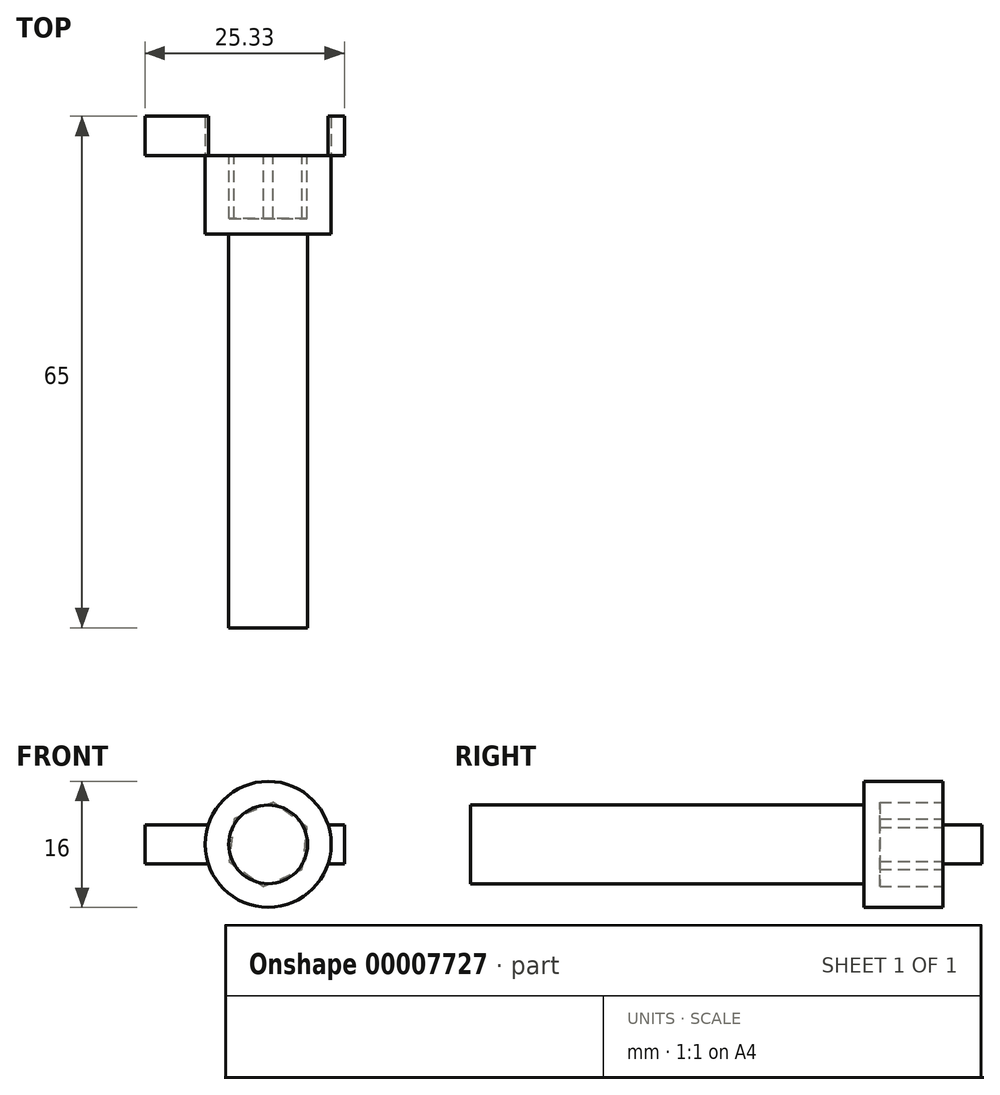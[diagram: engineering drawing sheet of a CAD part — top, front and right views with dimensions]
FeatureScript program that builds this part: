
annotation { "Feature Type Name" : "Feature", "Feature Type Description" : "" }
export const myFeature = defineFeature(function(context is Context, id is Id, definition is map)
    precondition{}
    {
        {
            var Q0;
            Q0=qCreatedBy(makeId("Right.planeOp"),FACE);
            var sketch = newSketch(context, id + "F0", { "sketchPlane" : qUnion([Q0])});
            skLineSegment(sketch, "E0", {"start": v(0, 0) * mm, "end": v(-60, 0) * mm});
            skLineSegment(sketch, "E1", {"start": v(-60, 0) * mm, "end": v(-60, 5) * mm});
            skLineSegment(sketch, "E2", {"start": v(-60, 5) * mm, "end": v(-10, 5) * mm});
            skLineSegment(sketch, "E3", {"start": v(-10, 5) * mm, "end": v(-10, 8) * mm});
            skLineSegment(sketch, "E4", {"start": v(-10, 8) * mm, "end": v(0, 8) * mm});
            skLineSegment(sketch, "E5", {"start": v(0, 8) * mm, "end": v(0, 0) * mm});
            skSolve(sketch);
        }
        {
            var Q0;
            Q0=makeQuery(id+"F0.imprint","IMPRINT",FACE,{"disambiguationData":[TD([[makeQuery(id+"F0.imprint","IMPRINT",EDGE,{"derivedFrom":sQuery(id+"F0.wireOp",EDGE,"E0")}),-1.0]])]});
            var Q1;
            Q1=sQuery(id+"F0.wireOp",EDGE,"E0");
            revolve(context, id + "F1", {"entities" : qUnion([Q0]), "axis" : qUnion([Q1]), "revolveType" : RevolveType.FULL});
        }
        {
            var Q0;
            Q0=makeQuery(id+"F1.opRevolve","SWEPT_FACE",FACE,{"disambiguationData":[OSD([sQuery(id+"F0.wireOp",EDGE,"E5")])]});
            var sketch = newSketch(context, id + "F2", { "sketchPlane" : qUnion([Q0])});
            skCircle(sketch, "E6.cCircle", {"center": v(0, 0) * mm, "radius": 4.67 * mm, "construction": true});
            skLineSegment(sketch, "E6.0", {"start": v(0.61, -5.35) * mm, "end": v(-4.33, -3.2) * mm});
            skLineSegment(sketch, "E6.1", {"start": v(-4.33, -3.2) * mm, "end": v(-4.94, 2.15) * mm});
            skLineSegment(sketch, "E6.2", {"start": v(-4.94, 2.15) * mm, "end": v(-0.61, 5.35) * mm});
            skLineSegment(sketch, "E6.3", {"start": v(-0.61, 5.35) * mm, "end": v(4.33, 3.2) * mm});
            skLineSegment(sketch, "E6.4", {"start": v(4.33, 3.2) * mm, "end": v(4.94, -2.15) * mm});
            skLineSegment(sketch, "E6.5", {"start": v(4.94, -2.15) * mm, "end": v(0.61, -5.35) * mm});
            skPoint(sketch, "E6.0.midPoint", {"position": v(-1.86, -4.28) * mm});
            skSolve(sketch);
        }
        {
            var Q0;
            Q0 = qSketchRegion(id + "F2", true);
            extrude(context, id + "F3", {"entities" : qUnion([Q0]), "operationType" : NewBodyOperationType.REMOVE, "oppositeDirection" : true, "depth" : 8 * mm});
        }
        {
            var Q0;
            Q0=makeQuery(id+"F1.opRevolve","SWEPT_FACE",FACE,{"disambiguationData":[OSD([sQuery(id+"F0.wireOp",EDGE,"E5")])]});
            var sketch = newSketch(context, id + "F4", { "sketchPlane" : qUnion([Q0])});
            skLineSegment(sketch, "E7.bottom", {"start": v(-9.69, 2.5) * mm, "end": v(15.64, 2.5) * mm});
            skLineSegment(sketch, "E7.top", {"start": v(-9.69, -2.5) * mm, "end": v(15.64, -2.5) * mm});
            skLineSegment(sketch, "E7.left", {"start": v(-9.69, 2.5) * mm, "end": v(-9.69, -2.5) * mm});
            skLineSegment(sketch, "E7.right", {"start": v(15.64, 2.5) * mm, "end": v(15.64, -2.5) * mm});
            skSolve(sketch);
        }
        {
            var Q0;
            {var subQ0=makeQuery(id+"F3.boolean.opBoolean","COPY",EDGE,{"derivedFrom":makeQuery(id+"F3.opExtrude","CAP_EDGE",EDGE,{"disambiguationData":[OSD([sQuery(id+"F2.wireOp",EDGE,"E6.2")])],"isStart":true})});var subQ3=makeQuery(id+"F3.boolean.opBoolean","COPY",EDGE,{"derivedFrom":makeQuery(id+"F3.opExtrude","CAP_EDGE",EDGE,{"disambiguationData":[OSD([sQuery(id+"F2.wireOp",EDGE,"E6.1")])],"isStart":true})});var subQ4=makeQuery(id+"F4.imprint","INTERSECT",VERTEX,{"derivedFrom":[subQ3,subQ0]});Q0=makeQuery(id+"F4.imprint","IMPRINT",FACE,{"disambiguationData":[TD([[makeQuery(id+"F4.imprint","IMPRINT",EDGE,{"disambiguationData":[TD([[subQ4,1.0]])],"derivedFrom":subQ3}),1.0]])]});}
            var Q1;
            {var subQ5=sQuery(id+"F4.wireOp",EDGE,"E7.left");Q1=makeQuery(id+"F4.imprint","IMPRINT",FACE,{"disambiguationData":[TD([[makeQuery(id+"F4.imprint","IMPRINT",EDGE,{"derivedFrom":subQ5}),1.0]])]});}
            var Q2;
            {var subQ5=makeQuery(id+"F3.boolean.opBoolean","COPY",EDGE,{"derivedFrom":makeQuery(id+"F3.opExtrude","CAP_EDGE",EDGE,{"disambiguationData":[OSD([sQuery(id+"F2.wireOp",EDGE,"E6.2")])],"isStart":true})});var subQ6=sQuery(id+"F4.wireOp",EDGE,"E7.bottom");var subQ7=makeQuery(id+"F4.imprint","INTERSECT",VERTEX,{"derivedFrom":[subQ5,subQ6]});Q2=makeQuery(id+"F4.imprint","IMPRINT",FACE,{"disambiguationData":[TD([[makeQuery(id+"F4.imprint","IMPRINT",EDGE,{"disambiguationData":[TD([[subQ7,-1.0]])],"derivedFrom":subQ6}),-1.0]])]});}
            var Q3;
            {var subQ5=sQuery(id+"F4.wireOp",EDGE,"E7.right");Q3=makeQuery(id+"F4.imprint","IMPRINT",FACE,{"disambiguationData":[TD([[makeQuery(id+"F4.imprint","IMPRINT",EDGE,{"derivedFrom":subQ5}),-1.0]])]});}
            extrude(context, id + "F5", {"entities" : qUnion([Q0, Q1, Q2, Q3]), "operationType" : NewBodyOperationType.ADD, "depth" : 5 * mm});
        }
    });
